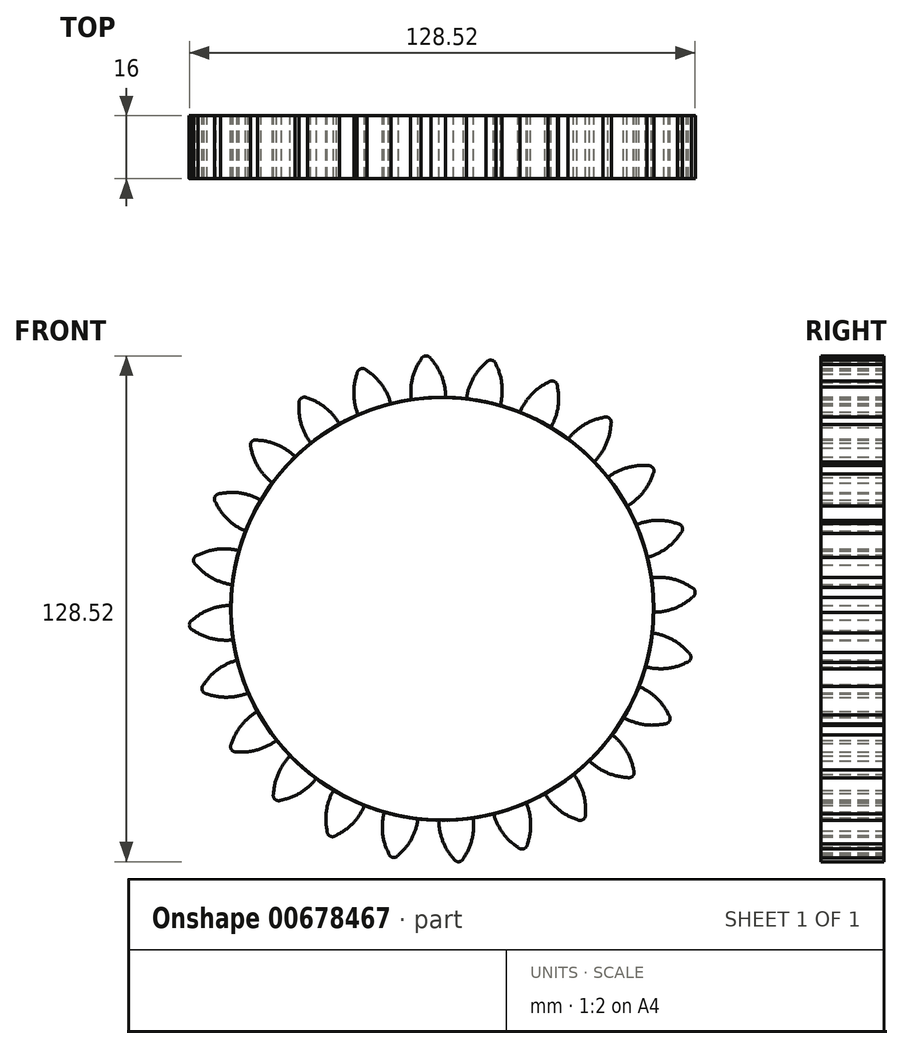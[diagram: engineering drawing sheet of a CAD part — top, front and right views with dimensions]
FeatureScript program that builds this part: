
annotation { "Feature Type Name" : "Feature", "Feature Type Description" : "" }
export const myFeature = defineFeature(function(context is Context, id is Id, definition is map)
    precondition{}
    {
        {
            var Q0;
            Q0=qCreatedBy(makeId("Front.planeOp"),FACE);
            var sketch = newSketch(context, id + "F0", { "sketchPlane" : qUnion([Q0])});
            skCircle(sketch, "E0", {"center": v(0, 0) * mm, "radius": 53.72 * mm});
            skCircle(sketch, "E1", {"center": v(0, 0) * mm, "radius": 58.67 * mm, "construction": true});
            skCircle(sketch, "E2", {"center": v(0, 0) * mm, "radius": 63.5 * mm, "construction": true});
            skLineSegment(sketch, "E3", {"start": v(0, 0) * mm, "end": v(0, 95.37) * mm, "construction": true});
            skLineSegment(sketch, "E4", {"start": v(0, 0) * mm, "end": v(-6.26, 95.47) * mm, "construction": true});
            skLineSegment(sketch, "E5", {"start": v(0, 58.67) * mm, "end": v(-48.27, 58.67) * mm, "construction": true});
            skLineSegment(sketch, "E6", {"start": v(0, 58.67) * mm, "end": v(-46.06, 41.9) * mm, "construction": true});
            skCircle(sketch, "E7", {"center": v(0, 0) * mm, "radius": 55.14 * mm, "construction": true});
            skCircle(sketch, "E8", {"center": v(0, 58.67) * mm, "radius": 14.6 * mm, "construction": true});
            skCircle(sketch, "E9", {"center": v(-13.72, 53.68) * mm, "radius": 14.6 * mm, "construction": true});
            skArc(sketch, "E10", {"start": v(0, 58.67) * mm, "mid": v(-1.2, 61.2) * mm, "end": v(-2.86, 63.44) * mm});
            skArc(sketch, "E11", {"start": v(0.88, 53.71) * mm, "mid": v(0.65, 56.23) * mm, "end": v(0, 58.67) * mm});
            skArc(sketch, "E12.MirrorCS", {"start": v(-7.66, 58.17) * mm, "mid": v(-6.8, 60.83) * mm, "end": v(-5.45, 63.27) * mm});
            skArc(sketch, "E13.MirrorCS", {"start": v(-7.88, 53.14) * mm, "mid": v(-7.98, 55.67) * mm, "end": v(-7.66, 58.17) * mm});
            skArc(sketch, "E14", {"start": v(-2.86, 63.44) * mm, "mid": v(-4.21, 64.26) * mm, "end": v(-5.45, 63.27) * mm});
            skSolve(sketch);
        }
        {
            var Q0;
            Q0=makeQuery(id+"F0.imprint","IMPRINT",FACE,{"disambiguationData":[TD([[makeQuery(id+"F0.imprint","IMPRINT",EDGE,{"derivedFrom":sQuery(id+"F0.wireOp",EDGE,"E10")}),1.0]])]});
            var Q1;
            {var subQ0=sQuery(id+"F0.wireOp",EDGE,"E0");var subQ1=makeQuery(id+"F0.imprint","INTERSECT",VERTEX,{"derivedFrom":[subQ0,sQuery(id+"F0.wireOp",EDGE,"E11")]});Q1=makeQuery(id+"F0.imprint","IMPRINT",FACE,{"disambiguationData":[TD([[makeQuery(id+"F0.imprint","IMPRINT",EDGE,{"disambiguationData":[TD([[subQ1,-1.0]])],"derivedFrom":subQ0}),1.0]])]});}
            extrude(context, id + "F1", {"entities" : qUnion([Q0, Q1]), "depth" : 16 * mm, "offsetDistance" : 25 * mm});
        }
        {
            var Q0;
            Q0=makeQuery(id+"F1.opExtrude","SWEPT_BODY",BODY,{"disambiguationData":[OSD([sQuery(id+"F0.wireOp",EDGE,"E0"),sQuery(id+"F0.wireOp",EDGE,"E10"),sQuery(id+"F0.wireOp",EDGE,"E11"),sQuery(id+"F0.wireOp",EDGE,"E12.MirrorCS"),sQuery(id+"F0.wireOp",EDGE,"E13.MirrorCS"),sQuery(id+"F0.wireOp",EDGE,"E14")])]});
            var Q1;
            Q1=makeQuery(id+"F1.opExtrude","SWEPT_FACE",FACE,{"disambiguationData":[OSD([sQuery(id+"F0.wireOp",EDGE,"E0")])]});
            circularPattern(context, id + "F2", {"entities" : qUnion([Q0]), "axis" : qUnion([Q1]), "angle" : 360 * degree, "instanceCount" : 24, "equalSpace" : true});
        }
    });
